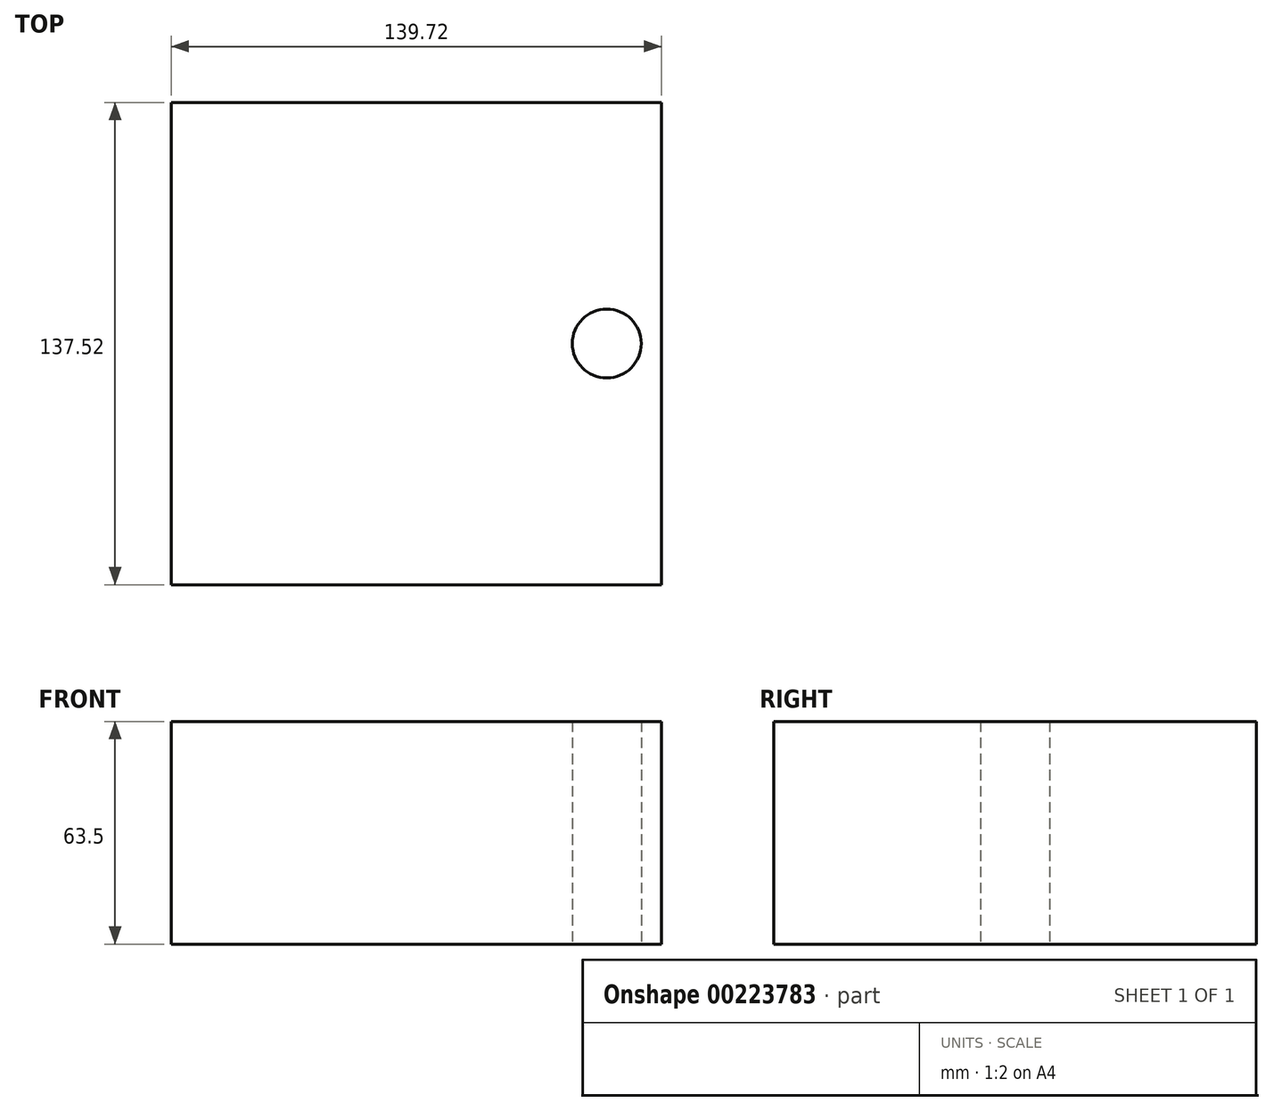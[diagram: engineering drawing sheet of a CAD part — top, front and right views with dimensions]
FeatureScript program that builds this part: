
annotation { "Feature Type Name" : "Feature", "Feature Type Description" : "" }
export const myFeature = defineFeature(function(context is Context, id is Id, definition is map)
    precondition{}
    {
        {
            var Q0;
            Q0=qCreatedBy(makeId("Top.planeOp"),FACE);
            var sketch = newSketch(context, id + "F0", { "sketchPlane" : qUnion([Q0])});
            skLineSegment(sketch, "E0.bottom", {"start": v(69.86, -68.76) * mm, "end": v(-69.86, -68.76) * mm});
            skLineSegment(sketch, "E0.top", {"start": v(69.86, 68.76) * mm, "end": v(-69.86, 68.76) * mm});
            skLineSegment(sketch, "E0.left", {"start": v(69.86, -68.76) * mm, "end": v(69.86, 68.76) * mm});
            skLineSegment(sketch, "E0.right", {"start": v(-69.86, -68.76) * mm, "end": v(-69.86, 68.76) * mm});
            skPoint(sketch, "E0.middle", {"position": v(0, 0) * mm});
            skLineSegment(sketch, "E1", {"start": v(0, 68.76) * mm, "end": v(0, -68.76) * mm});
            skSolve(sketch);
        }
        {
            var Q0;
            Q0=qCreatedBy(makeId("Top.planeOp"),FACE);
            var sketch = newSketch(context, id + "F1", { "sketchPlane" : qUnion([Q0])});
            skCircle(sketch, "E2", {"center": v(54.26, 0) * mm, "radius": 9.82 * mm});
            skSolve(sketch);
        }
        {
            var Q0;
            Q0=makeQuery(id+"F1.imprint","IMPRINT",FACE,{"disambiguationData":[TD([[makeQuery(id+"F1.imprint","IMPRINT",EDGE,{"derivedFrom":sQuery(id+"F1.wireOp",EDGE,"E2")}),1.0]])]});
            var Q1;
            {var subQ0=sQuery(id+"F0.wireOp",EDGE,"E0.left");Q1=makeQuery(id+"F0.imprint","IMPRINT",FACE,{"disambiguationData":[TD([[makeQuery(id+"F0.imprint","IMPRINT",EDGE,{"derivedFrom":subQ0}),1.0]])]});}
            var Q2;
            {var subQ0=sQuery(id+"F0.wireOp",EDGE,"E0.right");Q2=makeQuery(id+"F0.imprint","IMPRINT",FACE,{"disambiguationData":[TD([[makeQuery(id+"F0.imprint","IMPRINT",EDGE,{"derivedFrom":subQ0}),-1.0]])]});}
            extrude(context, id + "F2", {"entities" : qUnion([Q0, Q1, Q2]), "depth" : 63.5 * mm});
        }
        {
            var Q0;
            Q0=makeQuery(id+"F2.opExtrude","CAP_EDGE",EDGE,{"disambiguationData":[OSD([sQuery(id+"F1.wireOp",EDGE,"E2")])],"isStart":true});
            var Q1;
            Q1=sQuery(id+"F0.wireOp",EDGE,"E1");
            revolve(context, id + "F3", {"bodyType" : ToolBodyType.SURFACE, "surfaceEntities" : qUnion([Q0]), "axis" : qUnion([Q1]), "revolveType" : RevolveType.FULL});
        }
    });
